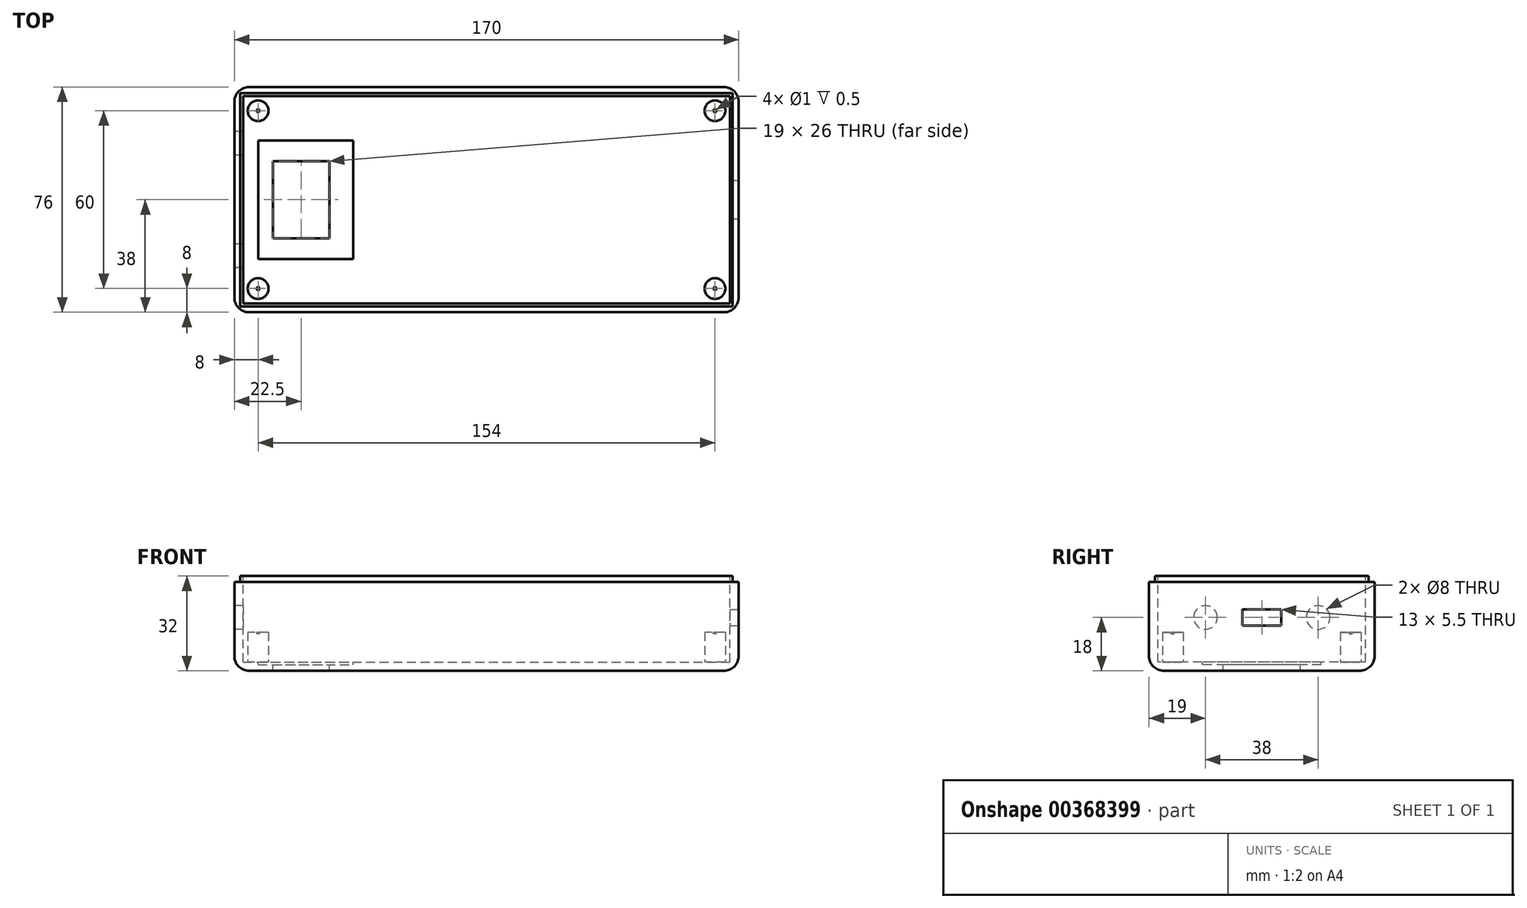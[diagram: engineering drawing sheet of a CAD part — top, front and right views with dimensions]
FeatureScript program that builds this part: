
annotation { "Feature Type Name" : "Feature", "Feature Type Description" : "" }
export const myFeature = defineFeature(function(context is Context, id is Id, definition is map)
    precondition{}
    {
        {
            var Q0;
            Q0=qCreatedBy(makeId("Top.planeOp"),FACE);
            var sketch = newSketch(context, id + "F0", { "sketchPlane" : qUnion([Q0])});
            skLineSegment(sketch, "E0.bottom", {"start": v(0, 0) * mm, "end": v(170, 0) * mm});
            skLineSegment(sketch, "E0.top", {"start": v(0, 76) * mm, "end": v(170, 76) * mm});
            skLineSegment(sketch, "E0.left", {"start": v(0, 0) * mm, "end": v(0, 76) * mm});
            skLineSegment(sketch, "E0.right", {"start": v(170, 0) * mm, "end": v(170, 76) * mm});
            skSolve(sketch);
        }
        {
            var Q0;
            Q0=qSketchRegion(id+"F0",true);
            extrude(context, id + "F1", {"entities" : qUnion([Q0]), "depth" : 30 * mm});
        }
        {
            var Q0;
            Q0=makeQuery(id+"F1.opExtrude","CAP_FACE",FACE,{"disambiguationData":[OSD([sQuery(id+"F0.wireOp",EDGE,"E0.bottom"),sQuery(id+"F0.wireOp",EDGE,"E0.top"),sQuery(id+"F0.wireOp",EDGE,"E0.left"),sQuery(id+"F0.wireOp",EDGE,"E0.right")])],"isStart":false});
            var sketch = newSketch(context, id + "F2", { "sketchPlane" : qUnion([Q0])});
            skLineSegment(sketch, "E1.bottom", {"start": v(3, 73) * mm, "end": v(167, 73) * mm});
            skLineSegment(sketch, "E1.top", {"start": v(3, 3) * mm, "end": v(167, 3) * mm});
            skLineSegment(sketch, "E1.left", {"start": v(3, 73) * mm, "end": v(3, 3) * mm});
            skLineSegment(sketch, "E1.right", {"start": v(167, 73) * mm, "end": v(167, 3) * mm});
            skSolve(sketch);
        }
        {
            var Q0;
            Q0=qSketchRegion(id+"F2",true);
            extrude(context, id + "F3", {"entities" : qUnion([Q0]), "operationType" : NewBodyOperationType.REMOVE, "oppositeDirection" : true, "depth" : 27 * mm});
        }
        {
            var Q0;
            Q0=makeQuery(id+"F3.boolean.opBoolean","COPY",FACE,{"derivedFrom":makeQuery(id+"F3.opExtrude","CAP_FACE",FACE,{"disambiguationData":[OSD([sQuery(id+"F2.wireOp",EDGE,"E1.bottom"),sQuery(id+"F2.wireOp",EDGE,"E1.top"),sQuery(id+"F2.wireOp",EDGE,"E1.left"),sQuery(id+"F2.wireOp",EDGE,"E1.right")])],"isStart":false})});
            var sketch = newSketch(context, id + "F4", { "sketchPlane" : qUnion([Q0])});
            skCircle(sketch, "E2", {"center": v(23, 68.5) * mm, "radius": 2.5 * mm});
            skCircle(sketch, "E3.0.1.0", {"center": v(23, 7.5) * mm, "radius": 2.5 * mm});
            skCircle(sketch, "E3.1.0.0", {"center": v(80.5, 68.5) * mm, "radius": 2.5 * mm});
            skCircle(sketch, "E3.1.1.0", {"center": v(80.5, 7.5) * mm, "radius": 2.5 * mm});
            skLineSegment(sketch, "E3.direction1", {"start": v(23, 68.5) * mm, "end": v(80.5, 68.5) * mm, "construction": true});
            skLineSegment(sketch, "E3.direction2", {"start": v(23, 68.5) * mm, "end": v(23, 7.5) * mm, "construction": true});
            skLineSegment(sketch, "E4", {"start": v(23, 38) * mm, "end": v(53.64, 38) * mm, "construction": true});
            skCircle(sketch, "E5", {"center": v(117, 68.5) * mm, "radius": 2.5 * mm});
            skCircle(sketch, "E6", {"center": v(148, 52.5) * mm, "radius": 2.5 * mm});
            skLineSegment(sketch, "E7", {"start": v(23, 7.5) * mm, "end": v(155.16, 7.5) * mm, "construction": true});
            skCircle(sketch, "E8.0.1.0", {"center": v(117, 23.5) * mm, "radius": 2.5 * mm});
            skCircle(sketch, "E8.0.1.1", {"center": v(148, 7.5) * mm, "radius": 2.5 * mm});
            skLineSegment(sketch, "E8.direction1", {"start": v(117, 68.5) * mm, "end": v(142, 68.5) * mm, "construction": true});
            skLineSegment(sketch, "E8.direction2", {"start": v(117, 68.5) * mm, "end": v(117, 23.5) * mm, "construction": true});
            skLineSegment(sketch, "E9", {"start": v(3, 38) * mm, "end": v(167, 38) * mm, "construction": true});
            skLineSegment(sketch, "E10.MirrorCS", {"start": v(168.2, 38) * mm, "end": v(11.2, 38) * mm, "construction": true});
            skSolve(sketch);
        }
        {
            var Q0;
            Q0=makeQuery(id+"F1.opExtrude","SWEPT_FACE",FACE,{"disambiguationData":[OSD([sQuery(id+"F0.wireOp",EDGE,"E0.left")])]});
            var sketch = newSketch(context, id + "F5", { "sketchPlane" : qUnion([Q0])});
            skCircle(sketch, "E11", {"center": v(-57, 18) * mm, "radius": 4 * mm});
            skLineSegment(sketch, "E12", {"start": v(-38, 30) * mm, "end": v(-38, 0) * mm, "construction": true});
            skCircle(sketch, "E13.MirrorC", {"center": v(-19, 18) * mm, "radius": 4 * mm});
            skSolve(sketch);
        }
        {
            var Q0;
            {var subQ0=sQuery(id+"F0.wireOp",EDGE,"E0.left");var subQ1=sQuery(id+"F0.wireOp",EDGE,"E0.top");var subQ2=sQuery(id+"F0.wireOp",EDGE,"E0.right");var subQ3=sQuery(id+"F0.wireOp",EDGE,"E0.bottom");Q0=makeQuery(id+"FoCSmkn9CXFEfcj_1.boolean.opBoolean","SPLIT",FACE,{"disambiguationData":[TD([makeQuery(id+"F1.opExtrude","SWEPT_FACE",FACE,{"disambiguationData":[OSD([subQ3])]}),makeQuery(id+"F1.opExtrude","SWEPT_FACE",FACE,{"disambiguationData":[OSD([subQ1])]}),makeQuery(id+"F1.opExtrude","SWEPT_FACE",FACE,{"disambiguationData":[OSD([subQ0])]}),makeQuery(id+"F1.opExtrude","SWEPT_FACE",FACE,{"disambiguationData":[OSD([subQ2])]}),makeQuery(id+"F3.boolean.opBoolean","COPY",FACE,{"derivedFrom":makeQuery(id+"F3.opExtrude","SWEPT_FACE",FACE,{"disambiguationData":[OSD([sQuery(id+"F2.wireOp",EDGE,"E1.bottom")])]})}),makeQuery(id+"F3.boolean.opBoolean","COPY",FACE,{"derivedFrom":makeQuery(id+"F3.opExtrude","SWEPT_FACE",FACE,{"disambiguationData":[OSD([sQuery(id+"F2.wireOp",EDGE,"E1.top")])]})}),makeQuery(id+"F3.boolean.opBoolean","COPY",FACE,{"derivedFrom":makeQuery(id+"F3.opExtrude","SWEPT_FACE",FACE,{"disambiguationData":[OSD([sQuery(id+"F2.wireOp",EDGE,"E1.left")])]})}),makeQuery(id+"F3.boolean.opBoolean","COPY",FACE,{"derivedFrom":makeQuery(id+"F3.opExtrude","SWEPT_FACE",FACE,{"disambiguationData":[OSD([sQuery(id+"F2.wireOp",EDGE,"E1.right")])]})}),makeQuery(id+"FoCSmkn9CXFEfcj_1.opExtrude","SWEPT_FACE",FACE,{"disambiguationData":[OSD([sQuery(id+"F5.wireOp",EDGE,"E11")])]}),makeQuery(id+"FoCSmkn9CXFEfcj_1.opExtrude","SWEPT_FACE",FACE,{"disambiguationData":[OSD([sQuery(id+"F5.wireOp",EDGE,"E13.MirrorC")])]})])],"derivedFrom":makeQuery(id+"F1.opExtrude","CAP_FACE",FACE,{"disambiguationData":[OSD([subQ3,subQ1,subQ0,subQ2])],"isStart":false})});}
            var sketch = newSketch(context, id + "F6", { "sketchPlane" : qUnion([Q0])});
            skLineSegment(sketch, "E14.bottom", {"start": v(2, 74) * mm, "end": v(168, 74) * mm});
            skLineSegment(sketch, "E14.top", {"start": v(2, 2) * mm, "end": v(168, 2) * mm});
            skLineSegment(sketch, "E14.left", {"start": v(2, 74) * mm, "end": v(2, 2) * mm});
            skLineSegment(sketch, "E14.right", {"start": v(168, 74) * mm, "end": v(168, 2) * mm});
            skLineSegment(sketch, "E15.bottom", {"start": v(3, 73) * mm, "end": v(167, 73) * mm});
            skLineSegment(sketch, "E15.top", {"start": v(3, 3) * mm, "end": v(167, 3) * mm});
            skLineSegment(sketch, "E15.left", {"start": v(3, 73) * mm, "end": v(3, 3) * mm});
            skLineSegment(sketch, "E15.right", {"start": v(167, 73) * mm, "end": v(167, 3) * mm});
            skSolve(sketch);
        }
        {
            var Q0;
            Q0=qSketchRegion(id+"F6",true);
            extrude(context, id + "F7", {"entities" : qUnion([Q0]), "operationType" : NewBodyOperationType.ADD, "depth" : 2 * mm});
        }
        {
            var Q0;
            Q0=makeQuery(id+"F4.imprint","IMPRINT",FACE,{"disambiguationData":[TD([[makeQuery(id+"F4.imprint","IMPRINT",EDGE,{"derivedFrom":sQuery(id+"F4.wireOp",EDGE,"E2")}),-1.0]])]});
            var sketch = newSketch(context, id + "F8", { "sketchPlane" : qUnion([Q0])});
            skCircle(sketch, "E16", {"center": v(8, 68) * mm, "radius": 3.5 * mm});
            skCircle(sketch, "E17.MirrorC", {"center": v(8, 8) * mm, "radius": 3.5 * mm});
            skCircle(sketch, "E18.1.0.0", {"center": v(162, 8) * mm, "radius": 3.5 * mm});
            skCircle(sketch, "E18.1.0.1", {"center": v(162, 68) * mm, "radius": 3.5 * mm});
            skLineSegment(sketch, "E18.direction1", {"start": v(8, 8) * mm, "end": v(162, 8) * mm, "construction": true});
            skSolve(sketch);
        }
        {
            var Q0;
            Q0=qSketchRegion(id+"F5",true);
            var Q1;
            Q1=makeQuery(id+"F7.boolean.opBoolean","MERGE",FACE,{"derivedFrom":[makeQuery(id+"F3.boolean.opBoolean","COPY",FACE,{"derivedFrom":makeQuery(id+"F3.opExtrude","SWEPT_FACE",FACE,{"disambiguationData":[OSD([sQuery(id+"F2.wireOp",EDGE,"E1.left")])]})}),makeQuery(id+"F7.opExtrude","SWEPT_FACE",FACE,{"disambiguationData":[OSD([sQuery(id+"F6.wireOp",EDGE,"E15.left")])]})]});
            extrude(context, id + "F9", {"entities" : qUnion([Q0]), "operationType" : NewBodyOperationType.REMOVE, "endBound" : BoundingType.UP_TO_SURFACE, "oppositeDirection" : true, "endBoundEntityFace" : qUnion([Q1]), "depth" : 25 * mm});
        }
        {
            var Q0;
            Q0=qSketchRegion(id+"F8",true);
            extrude(context, id + "F10", {"entities" : qUnion([Q0]), "operationType" : NewBodyOperationType.ADD, "depth" : 10 * mm});
        }
        {
            var Q0;
            Q0=makeQuery(id+"F10.opExtrude","CAP_FACE",FACE,{"disambiguationData":[OSD([sQuery(id+"F8.wireOp",EDGE,"E17.MirrorC")])],"isStart":false});
            var sketch = newSketch(context, id + "F11", { "sketchPlane" : qUnion([Q0])});
            skCircle(sketch, "E19", {"center": v(8, 68) * mm, "radius": 0.5 * mm});
            skCircle(sketch, "E20.0.1.0", {"center": v(8, 8) * mm, "radius": 0.5 * mm});
            skCircle(sketch, "E20.1.0.0", {"center": v(162, 68) * mm, "radius": 0.5 * mm});
            skCircle(sketch, "E20.1.1.0", {"center": v(162, 8) * mm, "radius": 0.5 * mm});
            skLineSegment(sketch, "E20.direction1", {"start": v(8, 68) * mm, "end": v(162, 68) * mm, "construction": true});
            skLineSegment(sketch, "E20.direction2", {"start": v(8, 68) * mm, "end": v(8, 8) * mm, "construction": true});
            skSolve(sketch);
        }
        {
            var Q0;
            Q0=makeQuery(id+"F11.imprint","IMPRINT",FACE,{"disambiguationData":[TD([[makeQuery(id+"F11.imprint","IMPRINT",EDGE,{"derivedFrom":sQuery(id+"F11.wireOp",EDGE,"E20.1.1.0")}),1.0]])]});
            var Q1;
            Q1=makeQuery(id+"F11.imprint","IMPRINT",FACE,{"disambiguationData":[TD([[makeQuery(id+"F11.imprint","IMPRINT",EDGE,{"derivedFrom":sQuery(id+"F11.wireOp",EDGE,"E20.0.1.0")}),1.0]])]});
            var Q2;
            Q2=makeQuery(id+"F11.imprint","IMPRINT",FACE,{"disambiguationData":[TD([[makeQuery(id+"F11.imprint","IMPRINT",EDGE,{"derivedFrom":sQuery(id+"F11.wireOp",EDGE,"E19")}),1.0]])]});
            var Q3;
            Q3=makeQuery(id+"F11.imprint","IMPRINT",FACE,{"disambiguationData":[TD([[makeQuery(id+"F11.imprint","IMPRINT",EDGE,{"derivedFrom":sQuery(id+"F11.wireOp",EDGE,"E20.1.0.0")}),1.0]])]});
            extrude(context, id + "F12", {"entities" : qUnion([Q0, Q1, Q2, Q3]), "operationType" : NewBodyOperationType.REMOVE, "oppositeDirection" : true, "depth" : 0.5 * mm});
        }
        {
            var Q0;
            Q0=makeQuery(id+"F1.opExtrude","SWEPT_FACE",FACE,{"disambiguationData":[OSD([sQuery(id+"F0.wireOp",EDGE,"E0.right")])]});
            var sketch = newSketch(context, id + "F13", { "sketchPlane" : qUnion([Q0])});
            skLineSegment(sketch, "E21", {"start": v(38, 30) * mm, "end": v(38, 0) * mm, "construction": true});
            skLineSegment(sketch, "E22.bottom", {"start": v(31.5, 20.75) * mm, "end": v(44.5, 20.75) * mm});
            skLineSegment(sketch, "E22.top", {"start": v(31.5, 15.25) * mm, "end": v(44.5, 15.25) * mm});
            skLineSegment(sketch, "E22.left", {"start": v(31.5, 20.75) * mm, "end": v(31.5, 15.25) * mm});
            skLineSegment(sketch, "E22.right", {"start": v(44.5, 20.75) * mm, "end": v(44.5, 15.25) * mm});
            skSolve(sketch);
        }
        {
            var Q0;
            Q0=qSketchRegion(id+"F13",true);
            var Q1;
            Q1=makeQuery(id+"F7.boolean.opBoolean","MERGE",FACE,{"derivedFrom":[makeQuery(id+"F3.boolean.opBoolean","COPY",FACE,{"derivedFrom":makeQuery(id+"F3.opExtrude","SWEPT_FACE",FACE,{"disambiguationData":[OSD([sQuery(id+"F2.wireOp",EDGE,"E1.right")])]})}),makeQuery(id+"F7.opExtrude","SWEPT_FACE",FACE,{"disambiguationData":[OSD([sQuery(id+"F6.wireOp",EDGE,"E15.right")])]})]});
            extrude(context, id + "F14", {"entities" : qUnion([Q0]), "operationType" : NewBodyOperationType.REMOVE, "endBound" : BoundingType.UP_TO_SURFACE, "oppositeDirection" : true, "endBoundEntityFace" : qUnion([Q1]), "depth" : 25 * mm});
        }
        {
            var Q0;
            Q0=makeQuery(id+"F1.opExtrude","CAP_EDGE",EDGE,{"disambiguationData":[OSD([sQuery(id+"F0.wireOp",EDGE,"E0.left")])],"isStart":true});
            var Q1;
            Q1=makeQuery(id+"F1.opExtrude","CAP_EDGE",EDGE,{"disambiguationData":[OSD([sQuery(id+"F0.wireOp",EDGE,"E0.top")])],"isStart":true});
            var Q2;
            Q2=makeQuery(id+"F1.opExtrude","CAP_EDGE",EDGE,{"disambiguationData":[OSD([sQuery(id+"F0.wireOp",EDGE,"E0.right")])],"isStart":true});
            var Q3;
            Q3=makeQuery(id+"F1.opExtrude","CAP_EDGE",EDGE,{"disambiguationData":[OSD([sQuery(id+"F0.wireOp",EDGE,"E0.bottom")])],"isStart":true});
            var Q4;
            Q4=makeQuery(id+"F1.opExtrude","SWEPT_EDGE",EDGE,{"disambiguationData":[OSD([sQuery(id+"F0.wireOp",EDGE,"E0.top"),sQuery(id+"F0.wireOp",EDGE,"E0.right")])]});
            var Q5;
            Q5=makeQuery(id+"F1.opExtrude","SWEPT_EDGE",EDGE,{"disambiguationData":[OSD([sQuery(id+"F0.wireOp",EDGE,"E0.bottom"),sQuery(id+"F0.wireOp",EDGE,"E0.right")])]});
            var Q6;
            Q6=makeQuery(id+"F1.opExtrude","SWEPT_EDGE",EDGE,{"disambiguationData":[OSD([sQuery(id+"F0.wireOp",EDGE,"E0.top"),sQuery(id+"F0.wireOp",EDGE,"E0.left")])]});
            var Q7;
            Q7=makeQuery(id+"F1.opExtrude","SWEPT_EDGE",EDGE,{"disambiguationData":[OSD([sQuery(id+"F0.wireOp",EDGE,"E0.bottom"),sQuery(id+"F0.wireOp",EDGE,"E0.left")])]});
            fillet(context, id + "F15", {"entities" : qUnion([Q0, Q1, Q2, Q3, Q4, Q5, Q6, Q7]), "radius" : 5 * mm, "tangentPropagation" : true, "allowEdgeOverflow" : false});
        }
        {
            var Q0;
            Q0=makeQuery(id+"F4.imprint","IMPRINT",FACE,{"disambiguationData":[TD([[makeQuery(id+"F4.imprint","IMPRINT",EDGE,{"derivedFrom":sQuery(id+"F4.wireOp",EDGE,"E2")}),-1.0]])]});
            var sketch = newSketch(context, id + "F16", { "sketchPlane" : qUnion([Q0])});
            skLineSegment(sketch, "E23.bottom", {"start": v(13, 51) * mm, "end": v(32, 51) * mm});
            skLineSegment(sketch, "E23.top", {"start": v(13, 25) * mm, "end": v(32, 25) * mm});
            skLineSegment(sketch, "E23.left", {"start": v(13, 51) * mm, "end": v(13, 25) * mm});
            skLineSegment(sketch, "E23.right", {"start": v(32, 51) * mm, "end": v(32, 25) * mm});
            skSolve(sketch);
        }
        {
            var Q0;
            Q0=qSketchRegion(id+"F16",true);
            extrude(context, id + "F17", {"entities" : qUnion([Q0]), "operationType" : NewBodyOperationType.REMOVE, "oppositeDirection" : true, "depth" : 25 * mm});
        }
        {
            var Q0;
            Q0=makeQuery(id+"F4.imprint","IMPRINT",FACE,{"disambiguationData":[TD([[makeQuery(id+"F4.imprint","IMPRINT",EDGE,{"derivedFrom":sQuery(id+"F4.wireOp",EDGE,"E2")}),-1.0]])]});
            var sketch = newSketch(context, id + "F18", { "sketchPlane" : qUnion([Q0])});
            skLineSegment(sketch, "E24.bottom", {"start": v(8, 58) * mm, "end": v(40, 58) * mm});
            skLineSegment(sketch, "E24.top", {"start": v(8, 18) * mm, "end": v(40, 18) * mm});
            skLineSegment(sketch, "E24.left", {"start": v(8, 58) * mm, "end": v(8, 18) * mm});
            skLineSegment(sketch, "E24.right", {"start": v(40, 58) * mm, "end": v(40, 18) * mm});
            skLineSegment(sketch, "E25.bottom", {"start": v(13, 51) * mm, "end": v(32, 51) * mm});
            skLineSegment(sketch, "E25.top", {"start": v(13, 25) * mm, "end": v(32, 25) * mm});
            skLineSegment(sketch, "E25.left", {"start": v(13, 51) * mm, "end": v(13, 25) * mm});
            skLineSegment(sketch, "E25.right", {"start": v(32, 51) * mm, "end": v(32, 25) * mm});
            skSolve(sketch);
        }
        {
            var Q0;
            Q0=qSketchRegion(id+"F18",true);
            extrude(context, id + "F19", {"entities" : qUnion([Q0]), "operationType" : NewBodyOperationType.REMOVE, "oppositeDirection" : true, "depth" : 1 * mm});
        }
    });
